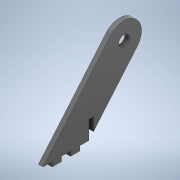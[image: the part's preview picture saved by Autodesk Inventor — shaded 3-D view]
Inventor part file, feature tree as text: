
AUTODESK INVENTOR PART (.ipt)
format: ipt  version: 2020 (Build 240168000, 168)  size: 128,000 bytes
history: native  units: in
note: dims shown in document units (in); Inventor stores cm internally (conversion verified against a paired STEP export)
features: extrude x2, sketch x2
ambient origin geometry x8: Origin, YZ Plane, XZ Plane, XY Plane, X Axis, Y Axis, Z Axis, Center Point
bodies: Solid1 (feature_tree)
feature tree (4):
  extrude  "Extrusion1"  Depth=0.1181in
  extrude  "Extrusion2"  Depth=0.1181in
  sketch  "Sketch1"  dims[d0=1.1811in d1=0.1181in]
  sketch  "Sketch3"  dims[d2=0.2362in d3=0.1181in d4=0.2362in d5=0.1181in d6=0.2362in d7=0.2362in d8=0.2362in d9=1.7717in d10=0.9055in d11=0.1181in d12=0.0in d13=0.2756in d14=0.3937in d15=0.0in d16=0.1181in]
